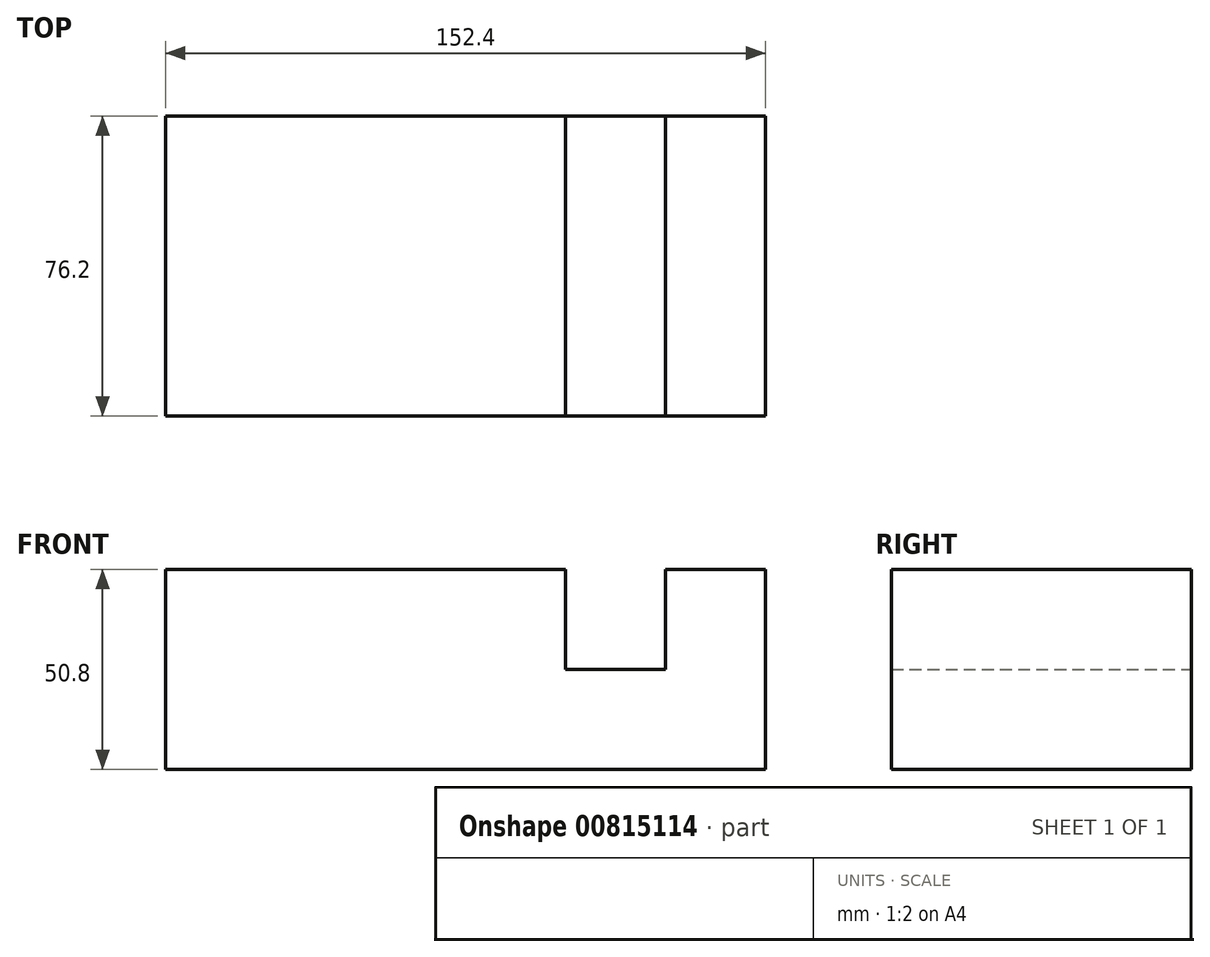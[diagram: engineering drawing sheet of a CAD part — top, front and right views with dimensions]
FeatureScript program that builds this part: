
annotation { "Feature Type Name" : "Feature", "Feature Type Description" : "" }
export const myFeature = defineFeature(function(context is Context, id is Id, definition is map)
    precondition{}
    {
        {
            var Q0;
            Q0=qCreatedBy(makeId("Front.planeOp"),FACE);
            var sketch = newSketch(context, id + "F0", { "sketchPlane" : qUnion([Q0])});
            skLineSegment(sketch, "E0", {"start": v(-69.23, 9.5) * mm, "end": v(83.17, 9.5) * mm});
            skLineSegment(sketch, "E1", {"start": v(83.17, 9.5) * mm, "end": v(83.17, 60.3) * mm});
            skLineSegment(sketch, "E2", {"start": v(83.17, 60.3) * mm, "end": v(57.77, 60.3) * mm});
            skLineSegment(sketch, "E3", {"start": v(57.77, 60.3) * mm, "end": v(57.77, 34.9) * mm});
            skLineSegment(sketch, "E4", {"start": v(57.77, 34.9) * mm, "end": v(32.37, 34.9) * mm});
            skLineSegment(sketch, "E5", {"start": v(32.37, 34.9) * mm, "end": v(32.37, 60.3) * mm});
            skLineSegment(sketch, "E6", {"start": v(32.37, 60.3) * mm, "end": v(-69.23, 60.3) * mm});
            skLineSegment(sketch, "E7", {"start": v(-69.23, 60.3) * mm, "end": v(-69.23, 9.5) * mm});
            skSolve(sketch);
        }
        {
            var Q0;
            Q0=makeQuery(id+"F0.imprint","IMPRINT",FACE,{"disambiguationData":[TD([[makeQuery(id+"F0.imprint","IMPRINT",EDGE,{"derivedFrom":sQuery(id+"F0.wireOp",EDGE,"E0")}),1.0]])]});
            extrude(context, id + "F1", {"entities" : qUnion([Q0]), "depth" : 76.2 * mm, "offsetDistance" : 25.4 * mm});
        }
    });
